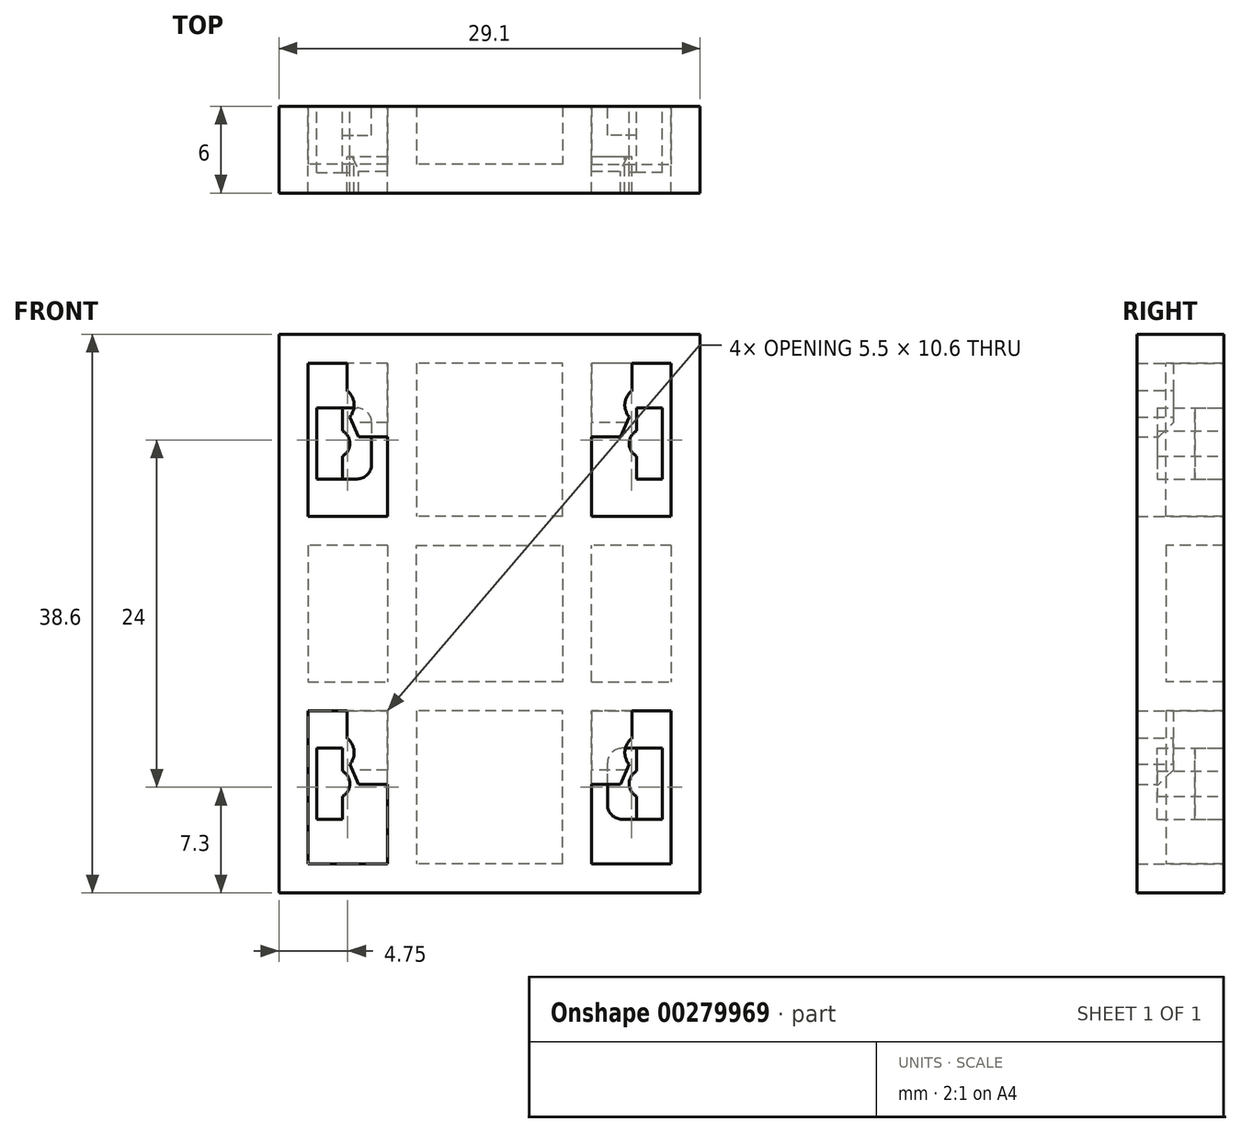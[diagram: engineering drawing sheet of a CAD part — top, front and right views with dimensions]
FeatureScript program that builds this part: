
annotation { "Feature Type Name" : "Feature", "Feature Type Description" : "" }
export const myFeature = defineFeature(function(context is Context, id is Id, definition is map)
    precondition{}
    {
        {
            var Q0;
            Q0=qCreatedBy(makeId("Front.planeOp"),FACE);
            var sketch = newSketch(context, id + "F0", { "sketchPlane" : qUnion([Q0])});
            skLineSegment(sketch, "E0.bottom", {"start": v(-11.95, 14.2) * mm, "end": v(-9.15, 14.2) * mm});
            skLineSegment(sketch, "E0.left", {"start": v(-11.95, 14.2) * mm, "end": v(-11.95, 9.3) * mm});
            skLineSegment(sketch, "E1", {"start": v(-11.95, 9.3) * mm, "end": v(-9.15, 9.3) * mm});
            skLineSegment(sketch, "E2", {"start": v(-8.15, 13.2) * mm, "end": v(-8.15, 10.3) * mm});
            skLineSegment(sketch, "E3", {"start": v(0, 35.81) * mm, "end": v(0, -29.5) * mm, "construction": true});
            skLineSegment(sketch, "E4", {"start": v(-33.5, 0) * mm, "end": v(32.4, 0) * mm, "construction": true});
            skLineSegment(sketch, "E5", {"start": v(-10.15, 14.2) * mm, "end": v(-10.15, 12.62) * mm});
            skArc(sketch, "E6", {"start": v(-10.15, 10.88) * mm, "mid": v(-9.65, 11.75) * mm, "end": v(-10.15, 12.62) * mm});
            skLineSegment(sketch, "E7.trimOffspring", {"start": v(-10.15, 10.88) * mm, "end": v(-10.15, 9.3) * mm});
            skPoint(sketch, "E8", {"position": v(-11.95, 11.75) * mm});
            skPoint(sketch, "E9.visualSharp", {"position": v(-8.15, 14.2) * mm});
            skArc(sketch, "E9.filletArc", {"start": v(-8.15, 13.2) * mm, "mid": v(-8.44, 13.9) * mm, "end": v(-9.15, 14.2) * mm});
            skPoint(sketch, "E10.visualSharp", {"position": v(-8.15, 9.3) * mm});
            skArc(sketch, "E10.filletArc", {"start": v(-9.15, 9.3) * mm, "mid": v(-8.44, 9.6) * mm, "end": v(-8.15, 10.3) * mm});
            skArc(sketch, "E11.MirrorCS", {"start": v(9.15, 9.3) * mm, "mid": v(8.44, 9.6) * mm, "end": v(8.15, 10.3) * mm});
            skLineSegment(sketch, "E12.MirrorCS", {"start": v(8.15, 13.2) * mm, "end": v(8.15, 10.3) * mm});
            skArc(sketch, "E13.MirrorCS", {"start": v(8.15, 13.2) * mm, "mid": v(8.44, 13.9) * mm, "end": v(9.15, 14.2) * mm});
            skLineSegment(sketch, "E14.MirrorCS", {"start": v(11.95, 14.2) * mm, "end": v(9.15, 14.2) * mm});
            skLineSegment(sketch, "E15.MirrorCS", {"start": v(11.95, 14.2) * mm, "end": v(11.95, 9.3) * mm});
            skLineSegment(sketch, "E16.MirrorCS", {"start": v(11.95, 9.3) * mm, "end": v(9.15, 9.3) * mm});
            skArc(sketch, "E17.MirrorCS", {"start": v(10.15, 10.88) * mm, "mid": v(9.65, 11.75) * mm, "end": v(10.15, 12.62) * mm});
            skLineSegment(sketch, "E18.MirrorCS", {"start": v(10.15, 14.2) * mm, "end": v(10.15, 12.62) * mm});
            skLineSegment(sketch, "E19.MirrorCS", {"start": v(10.15, 10.88) * mm, "end": v(10.15, 9.3) * mm});
            skLineSegment(sketch, "E20.MirrorCS", {"start": v(-11.95, -9.3) * mm, "end": v(-9.15, -9.3) * mm});
            skArc(sketch, "E21.MirrorCS", {"start": v(-9.15, -9.3) * mm, "mid": v(-8.44, -9.6) * mm, "end": v(-8.15, -10.3) * mm});
            skLineSegment(sketch, "E22.MirrorCS", {"start": v(-8.15, -13.2) * mm, "end": v(-8.15, -10.3) * mm});
            skArc(sketch, "E23.MirrorCS", {"start": v(-8.15, -13.2) * mm, "mid": v(-8.44, -13.9) * mm, "end": v(-9.15, -14.2) * mm});
            skLineSegment(sketch, "E24.MirrorCS", {"start": v(-11.95, -14.2) * mm, "end": v(-9.15, -14.2) * mm});
            skLineSegment(sketch, "E25.MirrorCS", {"start": v(-11.95, -14.2) * mm, "end": v(-11.95, -9.3) * mm});
            skLineSegment(sketch, "E26.MirrorCS", {"start": v(-10.15, -10.88) * mm, "end": v(-10.15, -9.3) * mm});
            skArc(sketch, "E27.MirrorCS", {"start": v(-10.15, -10.88) * mm, "mid": v(-9.65, -11.75) * mm, "end": v(-10.15, -12.62) * mm});
            skLineSegment(sketch, "E28.MirrorCS", {"start": v(-10.15, -14.2) * mm, "end": v(-10.15, -12.62) * mm});
            skArc(sketch, "E29.MirrorCS", {"start": v(9.15, -9.3) * mm, "mid": v(8.44, -9.6) * mm, "end": v(8.15, -10.3) * mm});
            skLineSegment(sketch, "E30.MirrorCS", {"start": v(11.95, -9.3) * mm, "end": v(9.15, -9.3) * mm});
            skLineSegment(sketch, "E31.MirrorCS", {"start": v(11.95, -14.2) * mm, "end": v(11.95, -9.3) * mm});
            skLineSegment(sketch, "E32.MirrorCS", {"start": v(11.95, -14.2) * mm, "end": v(9.15, -14.2) * mm});
            skArc(sketch, "E33.MirrorCS", {"start": v(8.15, -13.2) * mm, "mid": v(8.44, -13.9) * mm, "end": v(9.15, -14.2) * mm});
            skLineSegment(sketch, "E34.MirrorCS", {"start": v(8.15, -13.2) * mm, "end": v(8.15, -10.3) * mm});
            skLineSegment(sketch, "E35.MirrorCS", {"start": v(10.15, -14.2) * mm, "end": v(10.15, -12.62) * mm});
            skArc(sketch, "E36.MirrorCS", {"start": v(10.15, -10.88) * mm, "mid": v(9.65, -11.75) * mm, "end": v(10.15, -12.62) * mm});
            skLineSegment(sketch, "E37.MirrorCS", {"start": v(10.15, -10.88) * mm, "end": v(10.15, -9.3) * mm});
            skSolve(sketch);
        }
        {
            var Q0;
            {var subQ2=sQuery(id+"F0.wireOp",EDGE,"E0.left");Q0=makeQuery(id+"F0.imprint","IMPRINT",FACE,{"disambiguationData":[TD([[makeQuery(id+"F0.imprint","IMPRINT",EDGE,{"derivedFrom":subQ2}),1.0]])]});}
            var Q1;
            {var subQ1=sQuery(id+"F0.wireOp",EDGE,"E25.MirrorCS");Q1=makeQuery(id+"F0.imprint","IMPRINT",FACE,{"disambiguationData":[TD([[makeQuery(id+"F0.imprint","IMPRINT",EDGE,{"derivedFrom":subQ1}),-1.0]])]});}
            var Q2;
            {var subQ2=sQuery(id+"F0.wireOp",EDGE,"E31.MirrorCS");Q2=makeQuery(id+"F0.imprint","IMPRINT",FACE,{"disambiguationData":[TD([[makeQuery(id+"F0.imprint","IMPRINT",EDGE,{"derivedFrom":subQ2}),1.0]])]});}
            var Q3;
            {var subQ1=sQuery(id+"F0.wireOp",EDGE,"E15.MirrorCS");Q3=makeQuery(id+"F0.imprint","IMPRINT",FACE,{"disambiguationData":[TD([[makeQuery(id+"F0.imprint","IMPRINT",EDGE,{"derivedFrom":subQ1}),-1.0]])]});}
            extrude(context, id + "F1", {"entities" : qUnion([Q0, Q1, Q2, Q3]), "depth" : 4.6 * mm});
        }
        {
            var Q0;
            {var subQ1=sQuery(id+"F0.wireOp",EDGE,"E29.MirrorCS");Q0=makeQuery(id+"F0.imprint","IMPRINT",FACE,{"disambiguationData":[TD([[makeQuery(id+"F0.imprint","IMPRINT",EDGE,{"derivedFrom":subQ1}),1.0]])]});}
            var Q1;
            {var subQ3=sQuery(id+"F0.wireOp",EDGE,"E11.MirrorCS");Q1=makeQuery(id+"F0.imprint","IMPRINT",FACE,{"disambiguationData":[TD([[makeQuery(id+"F0.imprint","IMPRINT",EDGE,{"derivedFrom":subQ3}),-1.0]])]});}
            var Q2;
            Q2=makeQuery(id+"F0.imprint","IMPRINT",FACE,{"disambiguationData":[TD([[makeQuery(id+"F0.imprint","IMPRINT",EDGE,{"derivedFrom":sQuery(id+"F0.wireOp",EDGE,"E2")}),-1.0]])]});
            var Q3;
            {var subQ1=sQuery(id+"F0.wireOp",EDGE,"E21.MirrorCS");Q3=makeQuery(id+"F0.imprint","IMPRINT",FACE,{"disambiguationData":[TD([[makeQuery(id+"F0.imprint","IMPRINT",EDGE,{"derivedFrom":subQ1}),-1.0]])]});}
            extrude(context, id + "F2", {"entities" : qUnion([Q0, Q1, Q2, Q3]), "operationType" : NewBodyOperationType.ADD, "depth" : 2 * mm});
        }
        {
            var Q0;
            Q0=qCreatedBy(makeId("Front.planeOp"),FACE);
            var sketch = newSketch(context, id + "F3", { "sketchPlane" : qUnion([Q0])});
            skLineSegment(sketch, "E38.bottom", {"start": v(-12.55, 17.3) * mm, "end": v(-9.85, 17.3) * mm});
            skLineSegment(sketch, "E38.top", {"start": v(-12.55, 6.7) * mm, "end": v(-7.05, 6.7) * mm});
            skLineSegment(sketch, "E38.left", {"start": v(-12.55, 17.3) * mm, "end": v(-12.55, 6.7) * mm});
            skLineSegment(sketch, "E38.right", {"start": v(-7.05, 12.2) * mm, "end": v(-7.05, 6.7) * mm});
            skLineSegment(sketch, "E39", {"start": v(0, 46) * mm, "end": v(0, -46) * mm, "construction": true});
            skLineSegment(sketch, "E40", {"start": v(-39.5, 0) * mm, "end": v(39.5, 0) * mm, "construction": true});
            skLineSegment(sketch, "E41", {"start": v(-9.85, 17.3) * mm, "end": v(-9.85, 15.4) * mm});
            skArc(sketch, "E42", {"start": v(-9.65, 13.59) * mm, "mid": v(-9.36, 14.54) * mm, "end": v(-9.85, 15.4) * mm});
            skLineSegment(sketch, "E43", {"start": v(-9.65, 13.59) * mm, "end": v(-9.05, 12.2) * mm});
            skLineSegment(sketch, "E44", {"start": v(-9.05, 12.2) * mm, "end": v(-7.05, 12.2) * mm});
            skLineSegment(sketch, "E45.MirrorCS", {"start": v(7.05, 12.2) * mm, "end": v(7.05, 6.7) * mm});
            skLineSegment(sketch, "E46.MirrorCS", {"start": v(9.05, 12.2) * mm, "end": v(7.05, 12.2) * mm});
            skLineSegment(sketch, "E47.MirrorCS", {"start": v(9.65, 13.59) * mm, "end": v(9.05, 12.2) * mm});
            skArc(sketch, "E48.MirrorCS", {"start": v(9.65, 13.59) * mm, "mid": v(9.36, 14.54) * mm, "end": v(9.85, 15.4) * mm});
            skLineSegment(sketch, "E49.MirrorCS", {"start": v(9.85, 17.3) * mm, "end": v(9.85, 15.4) * mm});
            skLineSegment(sketch, "E50.MirrorCS", {"start": v(12.55, 17.3) * mm, "end": v(9.85, 17.3) * mm});
            skLineSegment(sketch, "E51.MirrorCS", {"start": v(12.55, 17.3) * mm, "end": v(12.55, 6.7) * mm});
            skLineSegment(sketch, "E52.MirrorCS", {"start": v(12.55, 6.7) * mm, "end": v(7.05, 6.7) * mm});
            skLineSegment(sketch, "E53.1.0.0", {"start": v(-12.55, -6.7) * mm, "end": v(-9.85, -6.7) * mm});
            skLineSegment(sketch, "E53.1.0.1", {"start": v(-12.55, -6.7) * mm, "end": v(-12.55, -17.3) * mm});
            skLineSegment(sketch, "E53.1.0.2", {"start": v(-12.55, -17.3) * mm, "end": v(-7.05, -17.3) * mm});
            skLineSegment(sketch, "E53.1.0.3", {"start": v(-7.05, -11.8) * mm, "end": v(-7.05, -17.3) * mm});
            skLineSegment(sketch, "E53.1.0.4", {"start": v(-9.05, -11.8) * mm, "end": v(-7.05, -11.8) * mm});
            skLineSegment(sketch, "E53.1.0.5", {"start": v(-9.65, -10.41) * mm, "end": v(-9.05, -11.8) * mm});
            skArc(sketch, "E53.1.0.6", {"start": v(-9.65, -10.41) * mm, "mid": v(-9.36, -9.46) * mm, "end": v(-9.85, -8.6) * mm});
            skLineSegment(sketch, "E53.1.0.7", {"start": v(-9.85, -6.7) * mm, "end": v(-9.85, -8.6) * mm});
            skLineSegment(sketch, "E53.1.0.8", {"start": v(12.55, -17.3) * mm, "end": v(7.05, -17.3) * mm});
            skLineSegment(sketch, "E53.1.0.9", {"start": v(7.05, -11.8) * mm, "end": v(7.05, -17.3) * mm});
            skLineSegment(sketch, "E53.1.0.10", {"start": v(9.05, -11.8) * mm, "end": v(7.05, -11.8) * mm});
            skLineSegment(sketch, "E53.1.0.11", {"start": v(9.65, -10.41) * mm, "end": v(9.05, -11.8) * mm});
            skArc(sketch, "E53.1.0.12", {"start": v(9.65, -10.41) * mm, "mid": v(9.36, -9.46) * mm, "end": v(9.85, -8.6) * mm});
            skLineSegment(sketch, "E53.1.0.13", {"start": v(9.85, -6.7) * mm, "end": v(9.85, -8.6) * mm});
            skLineSegment(sketch, "E53.1.0.14", {"start": v(12.55, -6.7) * mm, "end": v(9.85, -6.7) * mm});
            skLineSegment(sketch, "E53.1.0.15", {"start": v(12.55, -6.7) * mm, "end": v(12.55, -17.3) * mm});
            skLineSegment(sketch, "E53.direction1", {"start": v(-12.55, 6.7) * mm, "end": v(-12.55, -17.3) * mm, "construction": true});
            skLineSegment(sketch, "E54.bottom", {"start": v(14.55, 19.3) * mm, "end": v(-14.55, 19.3) * mm});
            skLineSegment(sketch, "E54.top", {"start": v(14.55, -19.3) * mm, "end": v(-14.55, -19.3) * mm});
            skLineSegment(sketch, "E54.left", {"start": v(14.55, 19.3) * mm, "end": v(14.55, -19.3) * mm});
            skLineSegment(sketch, "E54.right", {"start": v(-14.55, 19.3) * mm, "end": v(-14.55, -19.3) * mm});
            skSolve(sketch);
        }
        {
            var Q0;
            Q0 = qSketchRegion(id + "F3", true);
            extrude(context, id + "F4", {"entities" : qUnion([Q0]), "depth" : 6 * mm});
        }
        {
            var Q0;
            Q0=makeQuery(id+"F4.opExtrude","SWEPT_FACE",FACE,{"disambiguationData":[OSD([sQuery(id+"F3.wireOp",EDGE,"E53.1.0.10")])]});
            var Q1;
            Q1=makeQuery(id+"F4.opExtrude","SWEPT_FACE",FACE,{"disambiguationData":[OSD([sQuery(id+"F3.wireOp",EDGE,"E53.1.0.11")])]});
            var Q2;
            Q2=makeQuery(id+"F4.opExtrude","SWEPT_FACE",FACE,{"disambiguationData":[OSD([sQuery(id+"F3.wireOp",EDGE,"E53.1.0.12")])]});
            var Q3;
            Q3=makeQuery(id+"F4.opExtrude","SWEPT_FACE",FACE,{"disambiguationData":[OSD([sQuery(id+"F3.wireOp",EDGE,"E53.1.0.13")])]});
            var Q4;
            Q4=makeQuery(id+"F4.opExtrude","SWEPT_FACE",FACE,{"disambiguationData":[OSD([sQuery(id+"F3.wireOp",EDGE,"E46.MirrorCS")])]});
            var Q5;
            Q5=makeQuery(id+"F4.opExtrude","SWEPT_FACE",FACE,{"disambiguationData":[OSD([sQuery(id+"F3.wireOp",EDGE,"E47.MirrorCS")])]});
            var Q6;
            Q6=makeQuery(id+"F4.opExtrude","SWEPT_FACE",FACE,{"disambiguationData":[OSD([sQuery(id+"F3.wireOp",EDGE,"E48.MirrorCS")])]});
            var Q7;
            Q7=makeQuery(id+"F4.opExtrude","SWEPT_FACE",FACE,{"disambiguationData":[OSD([sQuery(id+"F3.wireOp",EDGE,"E49.MirrorCS")])]});
            var Q8;
            Q8=makeQuery(id+"F4.opExtrude","SWEPT_FACE",FACE,{"disambiguationData":[OSD([sQuery(id+"F3.wireOp",EDGE,"E53.1.0.4")])]});
            var Q9;
            Q9=makeQuery(id+"F4.opExtrude","SWEPT_FACE",FACE,{"disambiguationData":[OSD([sQuery(id+"F3.wireOp",EDGE,"E53.1.0.5")])]});
            var Q10;
            Q10=makeQuery(id+"F4.opExtrude","SWEPT_FACE",FACE,{"disambiguationData":[OSD([sQuery(id+"F3.wireOp",EDGE,"E53.1.0.6")])]});
            var Q11;
            Q11=makeQuery(id+"F4.opExtrude","SWEPT_FACE",FACE,{"disambiguationData":[OSD([sQuery(id+"F3.wireOp",EDGE,"E53.1.0.7")])]});
            var Q12;
            Q12=makeQuery(id+"F4.opExtrude","SWEPT_FACE",FACE,{"disambiguationData":[OSD([sQuery(id+"F3.wireOp",EDGE,"E44")])]});
            var Q13;
            Q13=makeQuery(id+"F4.opExtrude","SWEPT_FACE",FACE,{"disambiguationData":[OSD([sQuery(id+"F3.wireOp",EDGE,"E43")])]});
            var Q14;
            Q14=makeQuery(id+"F4.opExtrude","SWEPT_FACE",FACE,{"disambiguationData":[OSD([sQuery(id+"F3.wireOp",EDGE,"E42")])]});
            var Q15;
            Q15=makeQuery(id+"F4.opExtrude","SWEPT_FACE",FACE,{"disambiguationData":[OSD([sQuery(id+"F3.wireOp",EDGE,"E41")])]});
            var Q16;
            Q16=makeQuery(id+"F4.opExtrude","CAP_FACE",FACE,{"disambiguationData":[OSD([sQuery(id+"F3.wireOp",EDGE,"E38.bottom"),sQuery(id+"F3.wireOp",EDGE,"E38.top"),sQuery(id+"F3.wireOp",EDGE,"E38.left"),sQuery(id+"F3.wireOp",EDGE,"E38.right"),sQuery(id+"F3.wireOp",EDGE,"E41"),sQuery(id+"F3.wireOp",EDGE,"E42"),sQuery(id+"F3.wireOp",EDGE,"E43"),sQuery(id+"F3.wireOp",EDGE,"E44"),sQuery(id+"F3.wireOp",EDGE,"EqtDNg43-5zRr-Hm7a-FU9R-3LqhWgxcsYZT"),sQuery(id+"F3.wireOp",EDGE,"E45.MirrorCS"),sQuery(id+"F3.wireOp",EDGE,"E46.MirrorCS"),sQuery(id+"F3.wireOp",EDGE,"E47.MirrorCS"),sQuery(id+"F3.wireOp",EDGE,"E48.MirrorCS"),sQuery(id+"F3.wireOp",EDGE,"E49.MirrorCS"),sQuery(id+"F3.wireOp",EDGE,"E50.MirrorCS"),sQuery(id+"F3.wireOp",EDGE,"E51.MirrorCS"),sQuery(id+"F3.wireOp",EDGE,"E52.MirrorCS"),sQuery(id+"F3.wireOp",EDGE,"E53.1.0.0"),sQuery(id+"F3.wireOp",EDGE,"E53.1.0.1"),sQuery(id+"F3.wireOp",EDGE,"E53.1.0.2"),sQuery(id+"F3.wireOp",EDGE,"E53.1.0.3"),sQuery(id+"F3.wireOp",EDGE,"E53.1.0.4"),sQuery(id+"F3.wireOp",EDGE,"E53.1.0.5"),sQuery(id+"F3.wireOp",EDGE,"E53.1.0.6"),sQuery(id+"F3.wireOp",EDGE,"E53.1.0.7"),sQuery(id+"F3.wireOp",EDGE,"E53.1.0.8"),sQuery(id+"F3.wireOp",EDGE,"E53.1.0.9"),sQuery(id+"F3.wireOp",EDGE,"E53.1.0.10"),sQuery(id+"F3.wireOp",EDGE,"E53.1.0.11"),sQuery(id+"F3.wireOp",EDGE,"E53.1.0.12"),sQuery(id+"F3.wireOp",EDGE,"E53.1.0.13"),sQuery(id+"F3.wireOp",EDGE,"E53.1.0.14"),sQuery(id+"F3.wireOp",EDGE,"E53.1.0.15")])],"isStart":true});
            var Q17;
            Q17=makeQuery(id+"F4.opExtrude","SWEPT_FACE",FACE,{"disambiguationData":[OSD([sQuery(id+"F3.wireOp",EDGE,"E50.MirrorCS")])]});
            var Q18;
            Q18=makeQuery(id+"F4.opExtrude","SWEPT_FACE",FACE,{"disambiguationData":[OSD([sQuery(id+"F3.wireOp",EDGE,"E51.MirrorCS")])]});
            var Q19;
            Q19=makeQuery(id+"F4.opExtrude","SWEPT_FACE",FACE,{"disambiguationData":[OSD([sQuery(id+"F3.wireOp",EDGE,"E38.right")])]});
            var Q20;
            Q20=makeQuery(id+"F4.opExtrude","SWEPT_FACE",FACE,{"disambiguationData":[OSD([sQuery(id+"F3.wireOp",EDGE,"E38.bottom")])]});
            var Q21;
            Q21=makeQuery(id+"F4.opExtrude","SWEPT_FACE",FACE,{"disambiguationData":[OSD([sQuery(id+"F3.wireOp",EDGE,"E45.MirrorCS")])]});
            var Q22;
            Q22=makeQuery(id+"F4.opExtrude","SWEPT_FACE",FACE,{"disambiguationData":[OSD([sQuery(id+"F3.wireOp",EDGE,"E52.MirrorCS")])]});
            var Q23;
            Q23=makeQuery(id+"F4.opExtrude","SWEPT_FACE",FACE,{"disambiguationData":[OSD([sQuery(id+"F3.wireOp",EDGE,"E38.top")])]});
            var Q24;
            Q24=makeQuery(id+"F4.opExtrude","SWEPT_FACE",FACE,{"disambiguationData":[OSD([sQuery(id+"F3.wireOp",EDGE,"E38.left")])]});
            var Q25;
            Q25=makeQuery(id+"F4.opExtrude","SWEPT_FACE",FACE,{"disambiguationData":[OSD([sQuery(id+"F3.wireOp",EDGE,"E53.1.0.1")])]});
            var Q26;
            Q26=makeQuery(id+"F4.opExtrude","SWEPT_FACE",FACE,{"disambiguationData":[OSD([sQuery(id+"F3.wireOp",EDGE,"E53.1.0.2")])]});
            var Q27;
            Q27=makeQuery(id+"F4.opExtrude","SWEPT_FACE",FACE,{"disambiguationData":[OSD([sQuery(id+"F3.wireOp",EDGE,"E53.1.0.8")])]});
            var Q28;
            Q28=makeQuery(id+"F4.opExtrude","SWEPT_FACE",FACE,{"disambiguationData":[OSD([sQuery(id+"F3.wireOp",EDGE,"E53.1.0.9")])]});
            var Q29;
            Q29=makeQuery(id+"F4.opExtrude","SWEPT_FACE",FACE,{"disambiguationData":[OSD([sQuery(id+"F3.wireOp",EDGE,"E53.1.0.0")])]});
            var Q30;
            Q30=makeQuery(id+"F4.opExtrude","SWEPT_FACE",FACE,{"disambiguationData":[OSD([sQuery(id+"F3.wireOp",EDGE,"E53.1.0.3")])]});
            var Q31;
            Q31=makeQuery(id+"F4.opExtrude","SWEPT_FACE",FACE,{"disambiguationData":[OSD([sQuery(id+"F3.wireOp",EDGE,"E53.1.0.14")])]});
            var Q32;
            Q32=makeQuery(id+"F4.opExtrude","SWEPT_FACE",FACE,{"disambiguationData":[OSD([sQuery(id+"F3.wireOp",EDGE,"E53.1.0.15")])]});
            shell(context, id + "F5", {"entities" : qUnion([Q0, Q1, Q2, Q3, Q4, Q5, Q6, Q7, Q8, Q9, Q10, Q11, Q12, Q13, Q14, Q15, Q16, Q17, Q18, Q19, Q20, Q21, Q22, Q23, Q24, Q25, Q26, Q27, Q28, Q29, Q30, Q31, Q32]), "thickness" : 2 * mm});
        }
        {
            var Q0;
            {var subQ0=sQuery(id+"F3.wireOp",EDGE,"cPmULECz-mgiY-lQwV-Uy3N-2iKzfhs95w99");var subQ1=sQuery(id+"F3.wireOp",EDGE,"E53.1.0.15");var subQ2=sQuery(id+"F3.wireOp",EDGE,"E53.1.0.14");var subQ3=sQuery(id+"F3.wireOp",EDGE,"E53.1.0.13");var subQ4=sQuery(id+"F3.wireOp",EDGE,"E53.1.0.12");var subQ5=sQuery(id+"F3.wireOp",EDGE,"E53.1.0.11");var subQ6=sQuery(id+"F3.wireOp",EDGE,"E53.1.0.10");var subQ7=sQuery(id+"F3.wireOp",EDGE,"E53.1.0.9");var subQ8=sQuery(id+"F3.wireOp",EDGE,"E53.1.0.8");var subQ9=sQuery(id+"F3.wireOp",EDGE,"E53.1.0.7");var subQ10=sQuery(id+"F3.wireOp",EDGE,"E53.1.0.6");var subQ11=sQuery(id+"F3.wireOp",EDGE,"E53.1.0.5");var subQ12=sQuery(id+"F3.wireOp",EDGE,"E53.1.0.4");var subQ13=sQuery(id+"F3.wireOp",EDGE,"E53.1.0.3");var subQ14=sQuery(id+"F3.wireOp",EDGE,"E53.1.0.2");var subQ15=sQuery(id+"F3.wireOp",EDGE,"E53.1.0.1");var subQ16=sQuery(id+"F3.wireOp",EDGE,"E53.1.0.0");var subQ17=sQuery(id+"F3.wireOp",EDGE,"E52.MirrorCS");var subQ18=sQuery(id+"F3.wireOp",EDGE,"E51.MirrorCS");var subQ19=sQuery(id+"F3.wireOp",EDGE,"E50.MirrorCS");var subQ20=sQuery(id+"F3.wireOp",EDGE,"E49.MirrorCS");var subQ21=sQuery(id+"F3.wireOp",EDGE,"E48.MirrorCS");var subQ22=sQuery(id+"F3.wireOp",EDGE,"E47.MirrorCS");var subQ23=sQuery(id+"F3.wireOp",EDGE,"E46.MirrorCS");var subQ24=sQuery(id+"F3.wireOp",EDGE,"E45.MirrorCS");var subQ25=sQuery(id+"F3.wireOp",EDGE,"EqtDNg43-5zRr-Hm7a-FU9R-3LqhWgxcsYZT");var subQ26=sQuery(id+"F3.wireOp",EDGE,"E44");var subQ27=sQuery(id+"F3.wireOp",EDGE,"E43");var subQ28=sQuery(id+"F3.wireOp",EDGE,"E42");var subQ29=sQuery(id+"F3.wireOp",EDGE,"E41");var subQ30=sQuery(id+"F3.wireOp",EDGE,"E38.right");var subQ31=sQuery(id+"F3.wireOp",EDGE,"E38.left");var subQ32=sQuery(id+"F3.wireOp",EDGE,"E38.top");var subQ33=sQuery(id+"F3.wireOp",EDGE,"E38.bottom");Q0=makeQuery(id+"F5.opShell","OFFSET_FACE",FACE,{"disambiguationData":[OSD([subQ33,subQ32,subQ31,subQ30,subQ29,subQ28,subQ27,subQ26,subQ25,subQ24,subQ23,subQ22,subQ21,subQ20,subQ19,subQ18,subQ17,subQ16,subQ15,subQ14,subQ13,subQ12,subQ11,subQ10,subQ9,subQ8,subQ7,subQ6,subQ5,subQ4,subQ3,subQ2,subQ1,subQ0]),TDD([makeQuery(id+"F4.opExtrude","CAP_FACE",FACE,{"disambiguationData":[OSD([subQ33,subQ32,subQ31,subQ30,subQ29,subQ28,subQ27,subQ26,subQ25,subQ24,subQ23,subQ22,subQ21,subQ20,subQ19,subQ18,subQ17,subQ16,subQ15,subQ14,subQ13,subQ12,subQ11,subQ10,subQ9,subQ8,subQ7,subQ6,subQ5,subQ4,subQ3,subQ2,subQ1,subQ0])],"isStart":false})])]});}
            var sketch = newSketch(context, id + "F6", { "sketchPlane" : qUnion([Q0])});
            skLineSegment(sketch, "E55.0", {"start": v(-9.85, 17.3) * mm, "end": v(-9.85, 15.4) * mm});
            skArc(sketch, "E56.0", {"start": v(-9.65, 13.59) * mm, "mid": v(-9.36, 14.54) * mm, "end": v(-9.85, 15.4) * mm});
            skLineSegment(sketch, "E57.0", {"start": v(-9.65, 13.59) * mm, "end": v(-9.05, 12.2) * mm});
            skLineSegment(sketch, "E58.0", {"start": v(-9.05, 12.2) * mm, "end": v(-7.05, 12.2) * mm});
            skLineSegment(sketch, "E59.0", {"start": v(0, 46) * mm, "end": v(0, -46) * mm, "construction": true});
            skLineSegment(sketch, "E60.0", {"start": v(39.5, 0) * mm, "end": v(-39.5, 0) * mm, "construction": true});
            skLineSegment(sketch, "E61", {"start": v(-9.85, 17.3) * mm, "end": v(-7.05, 17.3) * mm});
            skLineSegment(sketch, "E62", {"start": v(-7.05, 17.3) * mm, "end": v(-7.05, 12.2) * mm});
            skLineSegment(sketch, "E63.MirrorCS", {"start": v(0, -11.4) * mm, "end": v(0, 80.6) * mm, "construction": true});
            skLineSegment(sketch, "E64.MirrorCS", {"start": v(7.05, 17.3) * mm, "end": v(7.05, 12.2) * mm});
            skLineSegment(sketch, "E65.MirrorCS", {"start": v(9.85, 17.3) * mm, "end": v(7.05, 17.3) * mm});
            skLineSegment(sketch, "E66.MirrorCS", {"start": v(9.85, 17.3) * mm, "end": v(9.85, 15.4) * mm});
            skArc(sketch, "E67.MirrorCS", {"start": v(9.65, 13.59) * mm, "mid": v(9.36, 14.54) * mm, "end": v(9.85, 15.4) * mm});
            skLineSegment(sketch, "E68.MirrorCS", {"start": v(9.65, 13.59) * mm, "end": v(9.05, 12.2) * mm});
            skLineSegment(sketch, "E69.MirrorCS", {"start": v(9.05, 12.2) * mm, "end": v(7.05, 12.2) * mm});
            skLineSegment(sketch, "E70.1.0.0", {"start": v(-9.05, -11.8) * mm, "end": v(-7.05, -11.8) * mm});
            skLineSegment(sketch, "E70.1.0.1", {"start": v(-9.65, -10.41) * mm, "end": v(-9.05, -11.8) * mm});
            skArc(sketch, "E70.1.0.2", {"start": v(-9.65, -10.41) * mm, "mid": v(-9.36, -9.46) * mm, "end": v(-9.85, -8.6) * mm});
            skLineSegment(sketch, "E70.1.0.3", {"start": v(-9.85, -6.7) * mm, "end": v(-9.85, -8.6) * mm});
            skLineSegment(sketch, "E70.1.0.4", {"start": v(-9.85, -6.7) * mm, "end": v(-7.05, -6.7) * mm});
            skLineSegment(sketch, "E70.1.0.5", {"start": v(-7.05, -6.7) * mm, "end": v(-7.05, -11.8) * mm});
            skLineSegment(sketch, "E70.1.0.6", {"start": v(7.05, -6.7) * mm, "end": v(7.05, -11.8) * mm});
            skLineSegment(sketch, "E70.1.0.7", {"start": v(9.05, -11.8) * mm, "end": v(7.05, -11.8) * mm});
            skLineSegment(sketch, "E70.1.0.8", {"start": v(9.65, -10.41) * mm, "end": v(9.05, -11.8) * mm});
            skArc(sketch, "E70.1.0.9", {"start": v(9.65, -10.41) * mm, "mid": v(9.36, -9.46) * mm, "end": v(9.85, -8.6) * mm});
            skLineSegment(sketch, "E70.1.0.10", {"start": v(9.85, -6.7) * mm, "end": v(9.85, -8.6) * mm});
            skLineSegment(sketch, "E70.1.0.11", {"start": v(9.85, -6.7) * mm, "end": v(7.05, -6.7) * mm});
            skLineSegment(sketch, "E70.direction1", {"start": v(-7.05, 12.2) * mm, "end": v(-7.05, -11.8) * mm, "construction": true});
            skSolve(sketch);
        }
        {
            var Q0;
            Q0 = qSketchRegion(id + "F6", true);
            extrude(context, id + "F7", {"entities" : qUnion([Q0]), "operationType" : NewBodyOperationType.ADD, "depth" : 0.5 * mm});
        }
        {
            var Q0;
            Q0=makeQuery(id+"F7.opExtrude","CAP_EDGE",EDGE,{"disambiguationData":[OSD([sQuery(id+"F6.wireOp",EDGE,"E70.1.0.0")])],"isStart":false});
            var Q1;
            Q1=makeQuery(id+"F7.opExtrude","CAP_EDGE",EDGE,{"disambiguationData":[OSD([sQuery(id+"F6.wireOp",EDGE,"E70.1.0.7")])],"isStart":false});
            var Q2;
            Q2=makeQuery(id+"F7.opExtrude","CAP_EDGE",EDGE,{"disambiguationData":[OSD([sQuery(id+"F6.wireOp",EDGE,"E69.MirrorCS")])],"isStart":false});
            var Q3;
            Q3=makeQuery(id+"F7.opExtrude","CAP_EDGE",EDGE,{"disambiguationData":[OSD([sQuery(id+"F6.wireOp",EDGE,"E58.0")])],"isStart":false});
            chamfer(context, id + "F8", {"entities" : qUnion([Q0, Q1, Q2, Q3]), "width" : 1 * mm, "tangentPropagation" : true});
        }
        {
            var Q0;
            Q0=makeQuery(id+"F5.opShell","OFFSET_FACE",FACE,{"disambiguationData":[OSD([sQuery(id+"F3.wireOp",EDGE,"E38.bottom"),sQuery(id+"F3.wireOp",EDGE,"E38.top"),sQuery(id+"F3.wireOp",EDGE,"E38.left"),sQuery(id+"F3.wireOp",EDGE,"E38.right"),sQuery(id+"F3.wireOp",EDGE,"E41"),sQuery(id+"F3.wireOp",EDGE,"E42"),sQuery(id+"F3.wireOp",EDGE,"E43"),sQuery(id+"F3.wireOp",EDGE,"E44"),sQuery(id+"F3.wireOp",EDGE,"E45.MirrorCS"),sQuery(id+"F3.wireOp",EDGE,"E46.MirrorCS"),sQuery(id+"F3.wireOp",EDGE,"E47.MirrorCS"),sQuery(id+"F3.wireOp",EDGE,"E48.MirrorCS"),sQuery(id+"F3.wireOp",EDGE,"E49.MirrorCS"),sQuery(id+"F3.wireOp",EDGE,"E50.MirrorCS"),sQuery(id+"F3.wireOp",EDGE,"E51.MirrorCS"),sQuery(id+"F3.wireOp",EDGE,"E52.MirrorCS"),sQuery(id+"F3.wireOp",EDGE,"E53.1.0.0"),sQuery(id+"F3.wireOp",EDGE,"E53.1.0.1"),sQuery(id+"F3.wireOp",EDGE,"E53.1.0.2"),sQuery(id+"F3.wireOp",EDGE,"E53.1.0.3"),sQuery(id+"F3.wireOp",EDGE,"E53.1.0.4"),sQuery(id+"F3.wireOp",EDGE,"E53.1.0.5"),sQuery(id+"F3.wireOp",EDGE,"E53.1.0.6"),sQuery(id+"F3.wireOp",EDGE,"E53.1.0.7"),sQuery(id+"F3.wireOp",EDGE,"E53.1.0.8"),sQuery(id+"F3.wireOp",EDGE,"E53.1.0.9"),sQuery(id+"F3.wireOp",EDGE,"E53.1.0.10"),sQuery(id+"F3.wireOp",EDGE,"E53.1.0.11"),sQuery(id+"F3.wireOp",EDGE,"E53.1.0.12"),sQuery(id+"F3.wireOp",EDGE,"E53.1.0.13"),sQuery(id+"F3.wireOp",EDGE,"E53.1.0.14"),sQuery(id+"F3.wireOp",EDGE,"E53.1.0.15"),sQuery(id+"F3.wireOp",EDGE,"E54.bottom"),sQuery(id+"F3.wireOp",EDGE,"E54.top"),sQuery(id+"F3.wireOp",EDGE,"E54.left"),sQuery(id+"F3.wireOp",EDGE,"E54.right")])]});
            var sketch = newSketch(context, id + "F9", { "sketchPlane" : qUnion([Q0])});
            skLineSegment(sketch, "E71.0.0", {"start": v(7.05, -11.3) * mm, "end": v(7.05, -6.7) * mm});
            skLineSegment(sketch, "E71.0.1", {"start": v(7.05, -6.7) * mm, "end": v(9.85, -6.7) * mm});
            skLineSegment(sketch, "E71.0.2", {"start": v(9.85, -6.7) * mm, "end": v(12.55, -6.7) * mm});
            skLineSegment(sketch, "E71.0.3", {"start": v(12.55, -6.7) * mm, "end": v(12.55, -4.7) * mm});
            skLineSegment(sketch, "E71.0.4", {"start": v(12.55, 6.7) * mm, "end": v(7.05, 6.7) * mm});
            skLineSegment(sketch, "E71.0.5", {"start": v(7.05, 6.7) * mm, "end": v(7.05, 12.7) * mm});
            skLineSegment(sketch, "E71.0.6", {"start": v(7.05, 12.7) * mm, "end": v(7.05, 17.3) * mm});
            skLineSegment(sketch, "E71.0.7", {"start": v(7.05, 17.3) * mm, "end": v(5.05, 17.3) * mm});
            skLineSegment(sketch, "E71.0.8", {"start": v(-7.05, 17.3) * mm, "end": v(-7.05, 12.7) * mm});
            skLineSegment(sketch, "E71.0.9", {"start": v(-7.05, 12.7) * mm, "end": v(-7.05, 6.7) * mm});
            skLineSegment(sketch, "E71.0.10", {"start": v(-7.05, 6.7) * mm, "end": v(-12.55, 6.7) * mm});
            skLineSegment(sketch, "E71.0.11", {"start": v(-12.55, 6.7) * mm, "end": v(-12.55, 4.7) * mm});
            skLineSegment(sketch, "E71.0.12", {"start": v(-12.55, -6.7) * mm, "end": v(-9.85, -6.7) * mm});
            skLineSegment(sketch, "E71.0.13", {"start": v(-9.85, -6.7) * mm, "end": v(-7.05, -6.7) * mm});
            skLineSegment(sketch, "E71.0.14", {"start": v(-7.05, -6.7) * mm, "end": v(-7.05, -11.3) * mm});
            skLineSegment(sketch, "E71.0.15", {"start": v(-7.05, -11.3) * mm, "end": v(-7.05, -17.3) * mm});
            skLineSegment(sketch, "E71.0.16", {"start": v(-7.05, -17.3) * mm, "end": v(-5.05, -17.3) * mm});
            skLineSegment(sketch, "E71.0.17", {"start": v(7.05, -17.3) * mm, "end": v(7.05, -11.3) * mm});
            skLineSegment(sketch, "E72", {"start": v(-12.55, 4.7) * mm, "end": v(-7.05, 4.7) * mm});
            skLineSegment(sketch, "E73", {"start": v(12.55, -4.7) * mm, "end": v(7.05, -4.7) * mm});
            skLineSegment(sketch, "E74", {"start": v(-5.05, -17.3) * mm, "end": v(-5.05, -6.7) * mm});
            skLineSegment(sketch, "E75", {"start": v(5.05, 17.3) * mm, "end": v(5.05, 6.7) * mm});
            skLineSegment(sketch, "E76", {"start": v(-7.05, -4.7) * mm, "end": v(-7.05, 4.7) * mm});
            skLineSegment(sketch, "E77", {"start": v(7.05, 4.7) * mm, "end": v(7.05, -4.7) * mm});
            skLineSegment(sketch, "E78", {"start": v(-5.05, 6.7) * mm, "end": v(5.05, 6.7) * mm});
            skLineSegment(sketch, "E79", {"start": v(-5.05, -6.7) * mm, "end": v(5.05, -6.7) * mm});
            skLineSegment(sketch, "E80.trimOffspring", {"start": v(-5.05, 17.3) * mm, "end": v(-7.05, 17.3) * mm});
            skLineSegment(sketch, "E81.trimOffspring", {"start": v(-5.05, 6.7) * mm, "end": v(-5.05, 17.3) * mm});
            skLineSegment(sketch, "E82.trimOffspring", {"start": v(-5.05, 4.7) * mm, "end": v(5.05, 4.7) * mm});
            skLineSegment(sketch, "E83.trimOffspring", {"start": v(-7.05, -4.7) * mm, "end": v(-12.55, -4.7) * mm});
            skLineSegment(sketch, "E84.trimOffspring", {"start": v(-12.55, -4.7) * mm, "end": v(-12.55, -6.7) * mm});
            skLineSegment(sketch, "E85.trimOffspring", {"start": v(-5.05, -4.7) * mm, "end": v(-5.05, 4.7) * mm});
            skLineSegment(sketch, "E86.trimOffspring", {"start": v(5.05, -17.3) * mm, "end": v(7.05, -17.3) * mm});
            skLineSegment(sketch, "E87.trimOffspring", {"start": v(5.05, -6.7) * mm, "end": v(5.05, -17.3) * mm});
            skLineSegment(sketch, "E88.trimOffspring", {"start": v(5.05, -4.7) * mm, "end": v(-5.05, -4.7) * mm});
            skLineSegment(sketch, "E89.trimOffspring", {"start": v(12.55, 4.7) * mm, "end": v(12.55, 6.7) * mm});
            skLineSegment(sketch, "E90.trimOffspring", {"start": v(5.05, 4.7) * mm, "end": v(5.05, -4.7) * mm});
            skLineSegment(sketch, "E91.trimOffspring", {"start": v(7.05, 4.7) * mm, "end": v(12.55, 4.7) * mm});
            skSolve(sketch);
        }
        {
            var Q0;
            Q0 = qSketchRegion(id + "F9", true);
            var Q1;
            Q1=makeQuery(id+"F4.opExtrude","CAP_FACE",FACE,{"disambiguationData":[OSD([sQuery(id+"F3.wireOp",EDGE,"E38.bottom"),sQuery(id+"F3.wireOp",EDGE,"E38.top"),sQuery(id+"F3.wireOp",EDGE,"E38.left"),sQuery(id+"F3.wireOp",EDGE,"E38.right"),sQuery(id+"F3.wireOp",EDGE,"E41"),sQuery(id+"F3.wireOp",EDGE,"E42"),sQuery(id+"F3.wireOp",EDGE,"E43"),sQuery(id+"F3.wireOp",EDGE,"E44"),sQuery(id+"F3.wireOp",EDGE,"E45.MirrorCS"),sQuery(id+"F3.wireOp",EDGE,"E46.MirrorCS"),sQuery(id+"F3.wireOp",EDGE,"E47.MirrorCS"),sQuery(id+"F3.wireOp",EDGE,"E48.MirrorCS"),sQuery(id+"F3.wireOp",EDGE,"E49.MirrorCS"),sQuery(id+"F3.wireOp",EDGE,"E50.MirrorCS"),sQuery(id+"F3.wireOp",EDGE,"E51.MirrorCS"),sQuery(id+"F3.wireOp",EDGE,"E52.MirrorCS"),sQuery(id+"F3.wireOp",EDGE,"E53.1.0.0"),sQuery(id+"F3.wireOp",EDGE,"E53.1.0.1"),sQuery(id+"F3.wireOp",EDGE,"E53.1.0.2"),sQuery(id+"F3.wireOp",EDGE,"E53.1.0.3"),sQuery(id+"F3.wireOp",EDGE,"E53.1.0.4"),sQuery(id+"F3.wireOp",EDGE,"E53.1.0.5"),sQuery(id+"F3.wireOp",EDGE,"E53.1.0.6"),sQuery(id+"F3.wireOp",EDGE,"E53.1.0.7"),sQuery(id+"F3.wireOp",EDGE,"E53.1.0.8"),sQuery(id+"F3.wireOp",EDGE,"E53.1.0.9"),sQuery(id+"F3.wireOp",EDGE,"E53.1.0.10"),sQuery(id+"F3.wireOp",EDGE,"E53.1.0.11"),sQuery(id+"F3.wireOp",EDGE,"E53.1.0.12"),sQuery(id+"F3.wireOp",EDGE,"E53.1.0.13"),sQuery(id+"F3.wireOp",EDGE,"E53.1.0.14"),sQuery(id+"F3.wireOp",EDGE,"E53.1.0.15"),sQuery(id+"F3.wireOp",EDGE,"E54.bottom"),sQuery(id+"F3.wireOp",EDGE,"E54.top"),sQuery(id+"F3.wireOp",EDGE,"E54.left"),sQuery(id+"F3.wireOp",EDGE,"E54.right")])],"isStart":true});
            extrude(context, id + "F10", {"entities" : qUnion([Q0]), "operationType" : NewBodyOperationType.ADD, "endBound" : BoundingType.UP_TO_SURFACE, "endBoundEntityFace" : qUnion([Q1]), "depth" : 25 * mm});
        }
    });
